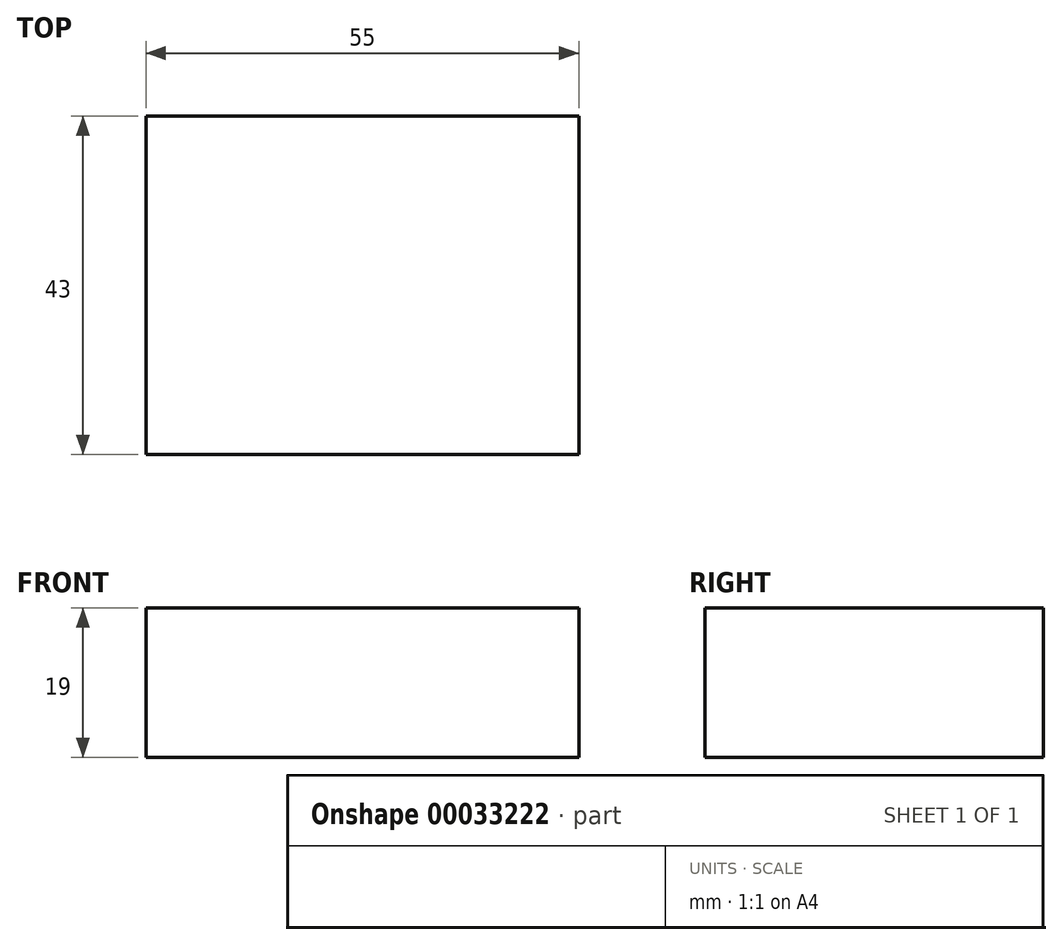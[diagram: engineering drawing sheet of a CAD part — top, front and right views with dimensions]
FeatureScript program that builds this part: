
annotation { "Feature Type Name" : "Feature", "Feature Type Description" : "" }
export const myFeature = defineFeature(function(context is Context, id is Id, definition is map)
    precondition{}
    {
        {
            var Q0;
            Q0=qCreatedBy(makeId("Top.planeOp"),FACE);
            var sketch = newSketch(context, id + "F0", { "sketchPlane" : qUnion([Q0])});
            skLineSegment(sketch, "E0.bottom", {"start": v(27.5, 21.5) * mm, "end": v(-27.5, 21.5) * mm});
            skLineSegment(sketch, "E0.top", {"start": v(27.5, -21.5) * mm, "end": v(-27.5, -21.5) * mm});
            skLineSegment(sketch, "E0.left", {"start": v(27.5, 21.5) * mm, "end": v(27.5, -21.5) * mm});
            skLineSegment(sketch, "E0.right", {"start": v(-27.5, 21.5) * mm, "end": v(-27.5, -21.5) * mm});
            skPoint(sketch, "E0.middle", {"position": v(0, 0) * mm});
            skSolve(sketch);
        }
        {
            var Q0;
            Q0 = qSketchRegion(id + "F0", true);
            extrude(context, id + "F1", {"entities" : qUnion([Q0]), "depth" : (19 / 2) * mm, "hasSecondDirection" : true, "secondDirectionOppositeDirection" : true, "secondDirectionDepth" : (19 / 2) * mm});
        }
    });
